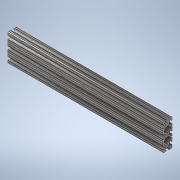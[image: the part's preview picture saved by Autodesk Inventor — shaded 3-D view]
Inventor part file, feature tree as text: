
AUTODESK INVENTOR PART (.ipt)
format: ipt  version: 2020 (Build 240168000, 168)  size: 380,416 bytes
history: native  units: in
note: dims shown in document units (in); Inventor stores cm internally (conversion verified against a paired STEP export)
features: sketch x2, extrude x1
ambient origin geometry x8: Origin, YZ Plane, XZ Plane, XY Plane, X Axis, Y Axis, Z Axis, Center Point
bodies: Solid1 (feature_tree)
feature tree (3):
  extrude  "Extrusion1"  [1 undecoded]
  sketch  "Sketch2"
  sketch  "Sketch1"  dims[d0=17.0in d1=0.0in]
note: 1 required parameter value undecoded (feature->parameter linkage not recoverable at this tier; creation-order binding heuristic only, values carry confidence <= 0.55)
